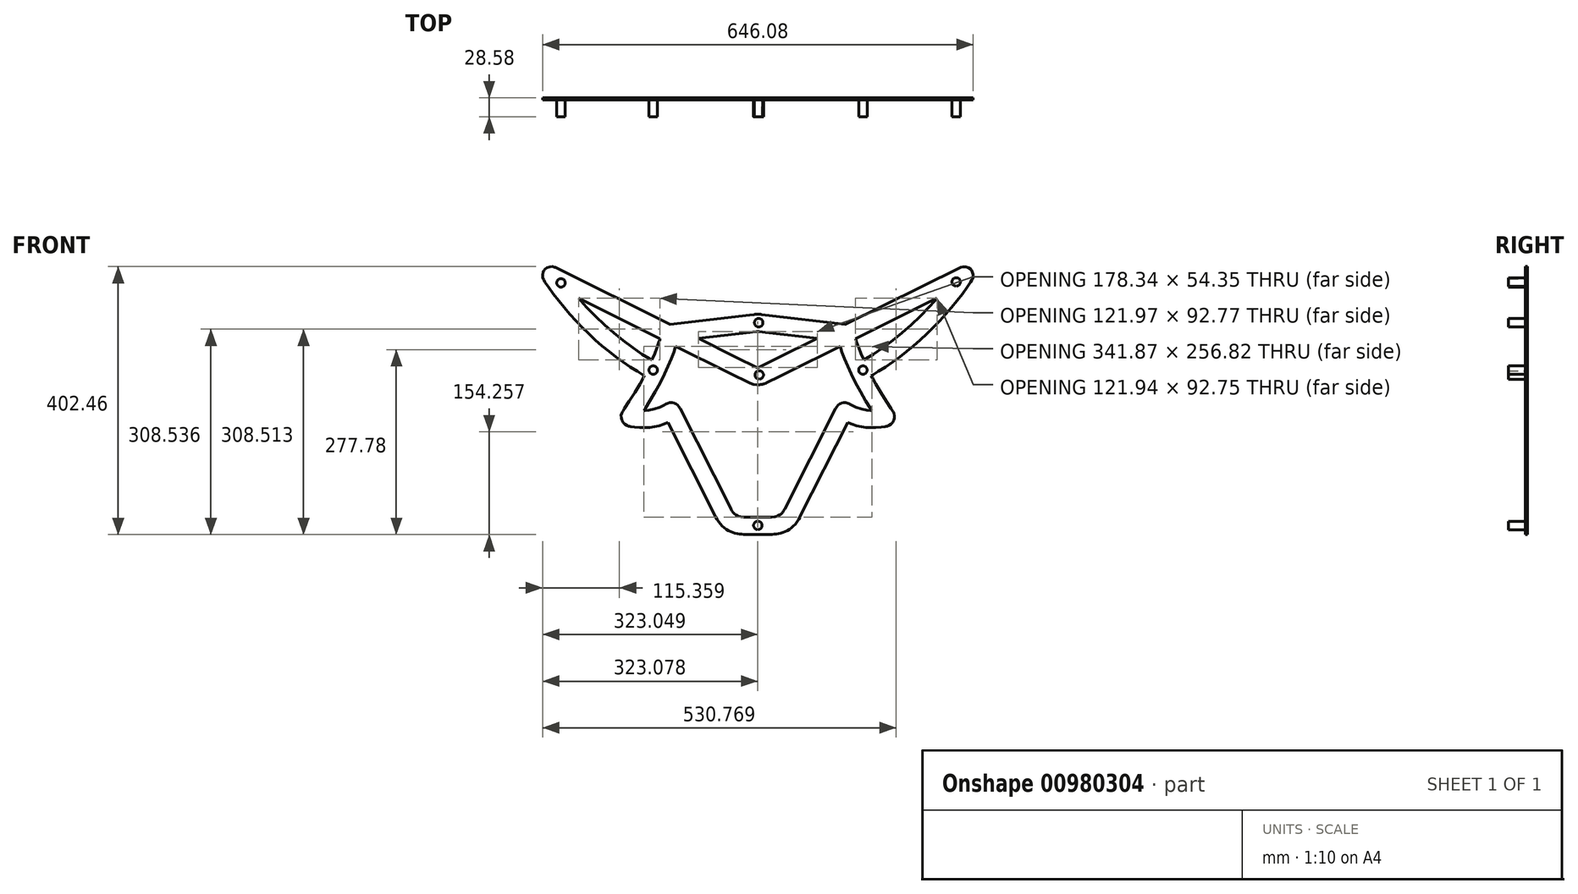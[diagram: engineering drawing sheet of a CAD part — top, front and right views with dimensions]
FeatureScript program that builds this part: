
annotation { "Feature Type Name" : "Feature", "Feature Type Description" : "" }
export const myFeature = defineFeature(function(context is Context, id is Id, definition is map)
    precondition{}
    {
        {
            var Q0;
            Q0=qCreatedBy(makeId("Front.planeOp"),FACE);
            var sketch = newSketch(context, id + "F0", { "sketchPlane" : qUnion([Q0])});
            skLineSegment(sketch, "E0", {"start": v(158.95, 60.93) * mm, "end": v(157.84, 63.41) * mm});
            skLineSegment(sketch, "E1", {"start": v(157.84, 63.41) * mm, "end": v(154.67, 70.92) * mm});
            skLineSegment(sketch, "E2", {"start": v(154.67, 70.92) * mm, "end": v(151.24, 79.68) * mm});
            skLineSegment(sketch, "E3", {"start": v(151.24, 79.68) * mm, "end": v(148.62, 87.1) * mm});
            skLineSegment(sketch, "E4", {"start": v(148.62, 87.1) * mm, "end": v(147.19, 91.58) * mm});
            skLineSegment(sketch, "E5", {"start": v(147.19, 91.58) * mm, "end": v(146.76, 93.08) * mm});
            skLineSegment(sketch, "E6", {"start": v(146.76, 93.08) * mm, "end": v(268.7, 153.68) * mm});
            skLineSegment(sketch, "E7", {"start": v(268.7, 153.68) * mm, "end": v(265.73, 150.2) * mm});
            skLineSegment(sketch, "E8", {"start": v(265.73, 150.2) * mm, "end": v(256.53, 140.02) * mm});
            skLineSegment(sketch, "E9", {"start": v(256.53, 140.02) * mm, "end": v(243.66, 126.71) * mm});
            skLineSegment(sketch, "E10", {"start": v(243.66, 126.71) * mm, "end": v(230.23, 113.88) * mm});
            skLineSegment(sketch, "E11", {"start": v(230.23, 113.88) * mm, "end": v(216.35, 101.64) * mm});
            skLineSegment(sketch, "E12", {"start": v(216.35, 101.64) * mm, "end": v(202.16, 90.1) * mm});
            skLineSegment(sketch, "E13", {"start": v(202.16, 90.1) * mm, "end": v(187.77, 79.4) * mm});
            skLineSegment(sketch, "E14", {"start": v(187.77, 79.4) * mm, "end": v(173.33, 69.63) * mm});
            skLineSegment(sketch, "E15", {"start": v(173.33, 69.63) * mm, "end": v(162.6, 63) * mm});
            skLineSegment(sketch, "E16", {"start": v(162.6, 63) * mm, "end": v(158.95, 60.93) * mm});
            skLineSegment(sketch, "E17", {"start": v(138.45, -5.62) * mm, "end": v(137.73, -5.16) * mm});
            skLineSegment(sketch, "E18", {"start": v(137.73, -5.16) * mm, "end": v(135.36, -4.11) * mm});
            skLineSegment(sketch, "E19", {"start": v(135.36, -4.11) * mm, "end": v(132.1, -3.33) * mm});
            skLineSegment(sketch, "E20", {"start": v(132.1, -3.33) * mm, "end": v(128.75, -3.29) * mm});
            skLineSegment(sketch, "E21", {"start": v(128.75, -3.29) * mm, "end": v(126.25, -3.73) * mm});
            skLineSegment(sketch, "E22", {"start": v(126.25, -3.73) * mm, "end": v(125.46, -4) * mm});
            skLineSegment(sketch, "E23", {"start": v(125.46, -4) * mm, "end": v(124.74, -4.23) * mm});
            skLineSegment(sketch, "E24", {"start": v(124.74, -4.23) * mm, "end": v(122.7, -5.25) * mm});
            skLineSegment(sketch, "E25", {"start": v(122.7, -5.25) * mm, "end": v(120.27, -7.02) * mm});
            skLineSegment(sketch, "E26", {"start": v(120.27, -7.02) * mm, "end": v(118.26, -9.24) * mm});
            skLineSegment(sketch, "E27", {"start": v(118.26, -9.24) * mm, "end": v(117.04, -11.17) * mm});
            skLineSegment(sketch, "E28", {"start": v(117.04, -11.17) * mm, "end": v(116.73, -11.86) * mm});
            skLineSegment(sketch, "E29", {"start": v(116.73, -11.86) * mm, "end": v(40.26, -162.76) * mm});
            skLineSegment(sketch, "E30", {"start": v(40.26, -162.76) * mm, "end": v(39.9, -163.51) * mm});
            skLineSegment(sketch, "E31", {"start": v(39.9, -163.51) * mm, "end": v(38.73, -165.7) * mm});
            skLineSegment(sketch, "E32", {"start": v(38.73, -165.7) * mm, "end": v(36.98, -168.27) * mm});
            skLineSegment(sketch, "E33", {"start": v(36.98, -168.27) * mm, "end": v(34.91, -170.44) * mm});
            skLineSegment(sketch, "E34", {"start": v(34.91, -170.44) * mm, "end": v(32.4, -172.21) * mm});
            skLineSegment(sketch, "E35", {"start": v(32.4, -172.21) * mm, "end": v(29.3, -173.6) * mm});
            skLineSegment(sketch, "E36", {"start": v(29.3, -173.6) * mm, "end": v(25.54, -174.59) * mm});
            skLineSegment(sketch, "E37", {"start": v(25.54, -174.59) * mm, "end": v(20.97, -175.19) * mm});
            skLineSegment(sketch, "E38", {"start": v(20.97, -175.19) * mm, "end": v(16.85, -175.38) * mm});
            skLineSegment(sketch, "E39", {"start": v(16.85, -175.38) * mm, "end": v(15.48, -175.38) * mm});
            skLineSegment(sketch, "E40", {"start": v(15.48, -175.38) * mm, "end": v(-15.4, -175.38) * mm});
            skLineSegment(sketch, "E41", {"start": v(-15.4, -175.38) * mm, "end": v(-16.77, -175.38) * mm});
            skLineSegment(sketch, "E42", {"start": v(-16.77, -175.38) * mm, "end": v(-20.88, -175.19) * mm});
            skLineSegment(sketch, "E43", {"start": v(-20.88, -175.19) * mm, "end": v(-25.46, -174.58) * mm});
            skLineSegment(sketch, "E44", {"start": v(-25.46, -174.58) * mm, "end": v(-29.24, -173.58) * mm});
            skLineSegment(sketch, "E45", {"start": v(-29.24, -173.58) * mm, "end": v(-32.34, -172.17) * mm});
            skLineSegment(sketch, "E46", {"start": v(-32.34, -172.17) * mm, "end": v(-34.88, -170.34) * mm});
            skLineSegment(sketch, "E47", {"start": v(-34.88, -170.34) * mm, "end": v(-36.99, -168.1) * mm});
            skLineSegment(sketch, "E48", {"start": v(-36.99, -168.1) * mm, "end": v(-38.78, -165.45) * mm});
            skLineSegment(sketch, "E49", {"start": v(-38.78, -165.45) * mm, "end": v(-40, -163.16) * mm});
            skLineSegment(sketch, "E50", {"start": v(-40, -163.16) * mm, "end": v(-40.37, -162.38) * mm});
            skLineSegment(sketch, "E51", {"start": v(-40.37, -162.38) * mm, "end": v(-116.64, -11.86) * mm});
            skLineSegment(sketch, "E52", {"start": v(-116.64, -11.86) * mm, "end": v(-116.96, -11.17) * mm});
            skLineSegment(sketch, "E53", {"start": v(-116.96, -11.17) * mm, "end": v(-118.19, -9.23) * mm});
            skLineSegment(sketch, "E54", {"start": v(-118.19, -9.23) * mm, "end": v(-120.2, -7) * mm});
            skLineSegment(sketch, "E55", {"start": v(-120.2, -7) * mm, "end": v(-122.63, -5.24) * mm});
            skLineSegment(sketch, "E56", {"start": v(-122.63, -5.24) * mm, "end": v(-124.68, -4.23) * mm});
            skLineSegment(sketch, "E57", {"start": v(-124.68, -4.23) * mm, "end": v(-125.4, -3.99) * mm});
            skLineSegment(sketch, "E58", {"start": v(-125.4, -3.99) * mm, "end": v(-126.2, -3.72) * mm});
            skLineSegment(sketch, "E59", {"start": v(-126.2, -3.72) * mm, "end": v(-128.7, -3.29) * mm});
            skLineSegment(sketch, "E60", {"start": v(-128.7, -3.29) * mm, "end": v(-132.04, -3.34) * mm});
            skLineSegment(sketch, "E61", {"start": v(-132.04, -3.34) * mm, "end": v(-135.3, -4.12) * mm});
            skLineSegment(sketch, "E62", {"start": v(-135.3, -4.12) * mm, "end": v(-137.66, -5.17) * mm});
            skLineSegment(sketch, "E63", {"start": v(-137.66, -5.17) * mm, "end": v(-138.37, -5.62) * mm});
            skLineSegment(sketch, "E64", {"start": v(-138.37, -5.62) * mm, "end": v(-140.4, -6.9) * mm});
            skLineSegment(sketch, "E65", {"start": v(-140.4, -6.9) * mm, "end": v(-146.9, -10.04) * mm});
            skLineSegment(sketch, "E66", {"start": v(-146.9, -10.04) * mm, "end": v(-155.32, -12.85) * mm});
            skLineSegment(sketch, "E67", {"start": v(-155.32, -12.85) * mm, "end": v(-163.4, -14.36) * mm});
            skLineSegment(sketch, "E68", {"start": v(-163.4, -14.36) * mm, "end": v(-169.02, -14.84) * mm});
            skLineSegment(sketch, "E69", {"start": v(-169.02, -14.84) * mm, "end": v(-170.9, -14.87) * mm});
            skLineSegment(sketch, "E70", {"start": v(-170.9, -14.87) * mm, "end": v(-168.58, -11.29) * mm});
            skLineSegment(sketch, "E71", {"start": v(-168.58, -11.29) * mm, "end": v(-161.87, -0.4) * mm});
            skLineSegment(sketch, "E72", {"start": v(-161.87, -0.4) * mm, "end": v(-153.74, 13.64) * mm});
            skLineSegment(sketch, "E73", {"start": v(-153.74, 13.64) * mm, "end": v(-146.5, 27.1) * mm});
            skLineSegment(sketch, "E74", {"start": v(-146.5, 27.1) * mm, "end": v(-140.15, 39.86) * mm});
            skLineSegment(sketch, "E75", {"start": v(-140.15, 39.86) * mm, "end": v(-134.66, 51.8) * mm});
            skLineSegment(sketch, "E76", {"start": v(-134.66, 51.8) * mm, "end": v(-130.02, 62.78) * mm});
            skLineSegment(sketch, "E77", {"start": v(-130.02, 62.78) * mm, "end": v(-126.23, 72.7) * mm});
            skLineSegment(sketch, "E78", {"start": v(-126.23, 72.7) * mm, "end": v(-123.96, 79.22) * mm});
            skLineSegment(sketch, "E79", {"start": v(-123.96, 79.22) * mm, "end": v(-123.27, 81.4) * mm});
            skLineSegment(sketch, "E80", {"start": v(-123.27, 81.4) * mm, "end": v(-44.12, 42.07) * mm});
            skLineSegment(sketch, "E81", {"start": v(-44.12, 42.07) * mm, "end": v(-44.12, 42.07) * mm});
            skLineSegment(sketch, "E82", {"start": v(-44.12, 42.07) * mm, "end": v(-41.36, 40.7) * mm});
            skLineSegment(sketch, "E83", {"start": v(-41.36, 40.7) * mm, "end": v(-12.8, 26.5) * mm});
            skLineSegment(sketch, "E84", {"start": v(-12.8, 26.5) * mm, "end": v(-11.81, 26.02) * mm});
            skLineSegment(sketch, "E85", {"start": v(-11.81, 26.02) * mm, "end": v(-6.56, 24.28) * mm});
            skLineSegment(sketch, "E86", {"start": v(-6.56, 24.28) * mm, "end": v(-1.6, 23.52) * mm});
            skLineSegment(sketch, "E87", {"start": v(-1.6, 23.52) * mm, "end": v(0.05, 23.52) * mm});
            skLineSegment(sketch, "E88", {"start": v(0.05, 23.52) * mm, "end": v(0.42, 23.52) * mm});
            skLineSegment(sketch, "E89", {"start": v(0.42, 23.52) * mm, "end": v(2.26, 23.7) * mm});
            skLineSegment(sketch, "E90", {"start": v(2.26, 23.7) * mm, "end": v(4.09, 23.99) * mm});
            skLineSegment(sketch, "E91", {"start": v(4.09, 23.99) * mm, "end": v(4.46, 24.05) * mm});
            skLineSegment(sketch, "E92", {"start": v(4.46, 24.05) * mm, "end": v(4.63, 24.08) * mm});
            skLineSegment(sketch, "E93", {"start": v(4.63, 24.08) * mm, "end": v(6.44, 24.26) * mm});
            skLineSegment(sketch, "E94", {"start": v(6.44, 24.26) * mm, "end": v(6.62, 24.3) * mm});
            skLineSegment(sketch, "E95", {"start": v(6.62, 24.3) * mm, "end": v(6.78, 24.34) * mm});
            skLineSegment(sketch, "E96", {"start": v(6.78, 24.34) * mm, "end": v(8.34, 24.93) * mm});
            skLineSegment(sketch, "E97", {"start": v(8.34, 24.93) * mm, "end": v(8.5, 24.98) * mm});
            skLineSegment(sketch, "E98", {"start": v(8.5, 24.98) * mm, "end": v(8.87, 25.09) * mm});
            skLineSegment(sketch, "E99", {"start": v(8.87, 25.09) * mm, "end": v(10.72, 25.67) * mm});
            skLineSegment(sketch, "E100", {"start": v(10.72, 25.67) * mm, "end": v(12.53, 26.37) * mm});
            skLineSegment(sketch, "E101", {"start": v(12.53, 26.37) * mm, "end": v(12.88, 26.54) * mm});
            skLineSegment(sketch, "E102", {"start": v(12.88, 26.54) * mm, "end": v(32.7, 36.4) * mm});
            skLineSegment(sketch, "E103", {"start": v(32.7, 36.4) * mm, "end": v(44.15, 42.08) * mm});
            skLineSegment(sketch, "E104", {"start": v(44.15, 42.08) * mm, "end": v(44.14, 42.08) * mm});
            skLineSegment(sketch, "E105", {"start": v(44.14, 42.08) * mm, "end": v(123.34, 81.44) * mm});
            skLineSegment(sketch, "E106", {"start": v(123.34, 81.44) * mm, "end": v(124.03, 79.25) * mm});
            skLineSegment(sketch, "E107", {"start": v(124.03, 79.25) * mm, "end": v(126.3, 72.72) * mm});
            skLineSegment(sketch, "E108", {"start": v(126.3, 72.72) * mm, "end": v(130.09, 62.8) * mm});
            skLineSegment(sketch, "E109", {"start": v(130.09, 62.8) * mm, "end": v(134.72, 51.81) * mm});
            skLineSegment(sketch, "E110", {"start": v(134.72, 51.81) * mm, "end": v(140.21, 39.87) * mm});
            skLineSegment(sketch, "E111", {"start": v(140.21, 39.87) * mm, "end": v(146.57, 27.1) * mm});
            skLineSegment(sketch, "E112", {"start": v(146.57, 27.1) * mm, "end": v(153.81, 13.65) * mm});
            skLineSegment(sketch, "E113", {"start": v(153.81, 13.65) * mm, "end": v(161.94, -0.39) * mm});
            skLineSegment(sketch, "E114", {"start": v(161.94, -0.39) * mm, "end": v(168.65, -11.29) * mm});
            skLineSegment(sketch, "E115", {"start": v(168.65, -11.29) * mm, "end": v(170.97, -14.87) * mm});
            skLineSegment(sketch, "E116", {"start": v(170.97, -14.87) * mm, "end": v(169.1, -14.84) * mm});
            skLineSegment(sketch, "E117", {"start": v(169.1, -14.84) * mm, "end": v(163.48, -14.36) * mm});
            skLineSegment(sketch, "E118", {"start": v(163.48, -14.36) * mm, "end": v(155.4, -12.85) * mm});
            skLineSegment(sketch, "E119", {"start": v(155.4, -12.85) * mm, "end": v(146.97, -10.04) * mm});
            skLineSegment(sketch, "E120", {"start": v(146.97, -10.04) * mm, "end": v(140.48, -6.89) * mm});
            skLineSegment(sketch, "E121", {"start": v(140.48, -6.89) * mm, "end": v(138.45, -5.62) * mm});
            skLineSegment(sketch, "E122", {"start": v(-268.67, 153.67) * mm, "end": v(-146.7, 93.05) * mm});
            skLineSegment(sketch, "E123", {"start": v(-146.7, 93.05) * mm, "end": v(-147.13, 91.55) * mm});
            skLineSegment(sketch, "E124", {"start": v(-147.13, 91.55) * mm, "end": v(-148.56, 87.07) * mm});
            skLineSegment(sketch, "E125", {"start": v(-148.56, 87.07) * mm, "end": v(-151.18, 79.64) * mm});
            skLineSegment(sketch, "E126", {"start": v(-151.18, 79.64) * mm, "end": v(-154.61, 70.88) * mm});
            skLineSegment(sketch, "E127", {"start": v(-154.61, 70.88) * mm, "end": v(-157.78, 63.38) * mm});
            skLineSegment(sketch, "E128", {"start": v(-157.78, 63.38) * mm, "end": v(-158.89, 60.9) * mm});
            skLineSegment(sketch, "E129", {"start": v(-158.89, 60.9) * mm, "end": v(-162.54, 62.97) * mm});
            skLineSegment(sketch, "E130", {"start": v(-162.54, 62.97) * mm, "end": v(-173.27, 69.6) * mm});
            skLineSegment(sketch, "E131", {"start": v(-173.27, 69.6) * mm, "end": v(-187.71, 79.36) * mm});
            skLineSegment(sketch, "E132", {"start": v(-187.71, 79.36) * mm, "end": v(-202.1, 90.07) * mm});
            skLineSegment(sketch, "E133", {"start": v(-202.1, 90.07) * mm, "end": v(-216.3, 101.6) * mm});
            skLineSegment(sketch, "E134", {"start": v(-216.3, 101.6) * mm, "end": v(-230.18, 113.85) * mm});
            skLineSegment(sketch, "E135", {"start": v(-230.18, 113.85) * mm, "end": v(-243.62, 126.69) * mm});
            skLineSegment(sketch, "E136", {"start": v(-243.62, 126.69) * mm, "end": v(-256.49, 140) * mm});
            skLineSegment(sketch, "E137", {"start": v(-256.49, 140) * mm, "end": v(-265.7, 150.19) * mm});
            skLineSegment(sketch, "E138", {"start": v(-265.7, 150.19) * mm, "end": v(-268.67, 153.67) * mm});
            skLineSegment(sketch, "E139", {"start": v(-11.4, 102.56) * mm, "end": v(-11.4, 102.56) * mm});
            skLineSegment(sketch, "E140", {"start": v(-11.4, 102.56) * mm, "end": v(-7.8, 103) * mm});
            skLineSegment(sketch, "E141", {"start": v(-7.8, 103) * mm, "end": v(-2.03, 103.68) * mm});
            skLineSegment(sketch, "E142", {"start": v(-2.03, 103.68) * mm, "end": v(-1.68, 103.72) * mm});
            skLineSegment(sketch, "E143", {"start": v(-1.68, 103.72) * mm, "end": v(1.76, 103.73) * mm});
            skLineSegment(sketch, "E144", {"start": v(1.76, 103.73) * mm, "end": v(2.1, 103.68) * mm});
            skLineSegment(sketch, "E145", {"start": v(2.1, 103.68) * mm, "end": v(6.66, 103.14) * mm});
            skLineSegment(sketch, "E146", {"start": v(6.66, 103.14) * mm, "end": v(11.48, 102.56) * mm});
            skLineSegment(sketch, "E147", {"start": v(11.48, 102.56) * mm, "end": v(11.48, 102.56) * mm});
            skLineSegment(sketch, "E148", {"start": v(11.48, 102.56) * mm, "end": v(89.18, 93.31) * mm});
            skLineSegment(sketch, "E149", {"start": v(89.18, 93.31) * mm, "end": v(27.84, 62.83) * mm});
            skLineSegment(sketch, "E150", {"start": v(27.84, 62.83) * mm, "end": v(1.36, 49.69) * mm});
            skLineSegment(sketch, "E151", {"start": v(1.36, 49.69) * mm, "end": v(1.25, 49.63) * mm});
            skLineSegment(sketch, "E152", {"start": v(1.25, 49.63) * mm, "end": v(0.3, 49.37) * mm});
            skLineSegment(sketch, "E153", {"start": v(0.3, 49.37) * mm, "end": v(-0.02, 49.37) * mm});
            skLineSegment(sketch, "E154", {"start": v(-0.02, 49.37) * mm, "end": v(-0.13, 49.38) * mm});
            skLineSegment(sketch, "E155", {"start": v(-0.13, 49.38) * mm, "end": v(-1.24, 49.64) * mm});
            skLineSegment(sketch, "E156", {"start": v(-1.24, 49.64) * mm, "end": v(-1.34, 49.7) * mm});
            skLineSegment(sketch, "E157", {"start": v(-1.34, 49.7) * mm, "end": v(-32.64, 65.22) * mm});
            skLineSegment(sketch, "E158", {"start": v(-32.64, 65.22) * mm, "end": v(-89.16, 93.3) * mm});
            skLineSegment(sketch, "E159", {"start": v(-89.16, 93.3) * mm, "end": v(-11.4, 102.56) * mm});
            skLineSegment(sketch, "E160", {"start": v(319.65, 196.96) * mm, "end": v(318.9, 197.75) * mm});
            skLineSegment(sketch, "E161", {"start": v(318.9, 197.75) * mm, "end": v(316.1, 199.63) * mm});
            skLineSegment(sketch, "E162", {"start": v(316.1, 199.63) * mm, "end": v(311.99, 201.03) * mm});
            skLineSegment(sketch, "E163", {"start": v(311.99, 201.03) * mm, "end": v(307.64, 201.1) * mm});
            skLineSegment(sketch, "E164", {"start": v(307.64, 201.1) * mm, "end": v(304.38, 200.27) * mm});
            skLineSegment(sketch, "E165", {"start": v(304.38, 200.27) * mm, "end": v(303.4, 199.78) * mm});
            skLineSegment(sketch, "E166", {"start": v(303.4, 199.78) * mm, "end": v(131.42, 114.3) * mm});
            skLineSegment(sketch, "E167", {"start": v(131.42, 114.3) * mm, "end": v(11.14, 128.63) * mm});
            skLineSegment(sketch, "E168", {"start": v(11.14, 128.63) * mm, "end": v(5.2, 129.34) * mm});
            skLineSegment(sketch, "E169", {"start": v(5.2, 129.34) * mm, "end": v(4.78, 129.39) * mm});
            skLineSegment(sketch, "E170", {"start": v(4.78, 129.39) * mm, "end": v(0.47, 129.64) * mm});
            skLineSegment(sketch, "E171", {"start": v(0.47, 129.64) * mm, "end": v(0.04, 129.64) * mm});
            skLineSegment(sketch, "E172", {"start": v(0.04, 129.64) * mm, "end": v(-0.4, 129.64) * mm});
            skLineSegment(sketch, "E173", {"start": v(-0.4, 129.64) * mm, "end": v(-4.71, 129.39) * mm});
            skLineSegment(sketch, "E174", {"start": v(-4.71, 129.39) * mm, "end": v(-5.14, 129.34) * mm});
            skLineSegment(sketch, "E175", {"start": v(-5.14, 129.34) * mm, "end": v(-12.44, 128.46) * mm});
            skLineSegment(sketch, "E176", {"start": v(-12.44, 128.46) * mm, "end": v(-131.4, 114.3) * mm});
            skLineSegment(sketch, "E177", {"start": v(-131.4, 114.3) * mm, "end": v(-303.73, 199.95) * mm});
            skLineSegment(sketch, "E178", {"start": v(-303.73, 199.95) * mm, "end": v(-304.7, 200.43) * mm});
            skLineSegment(sketch, "E179", {"start": v(-304.7, 200.43) * mm, "end": v(-307.9, 201.23) * mm});
            skLineSegment(sketch, "E180", {"start": v(-307.9, 201.23) * mm, "end": v(-312.18, 201.11) * mm});
            skLineSegment(sketch, "E181", {"start": v(-312.18, 201.11) * mm, "end": v(-316.2, 199.66) * mm});
            skLineSegment(sketch, "E182", {"start": v(-316.2, 199.66) * mm, "end": v(-318.9, 197.74) * mm});
            skLineSegment(sketch, "E183", {"start": v(-318.9, 197.74) * mm, "end": v(-319.63, 196.94) * mm});
            skLineSegment(sketch, "E184", {"start": v(-319.63, 196.94) * mm, "end": v(-319.9, 196.62) * mm});
            skLineSegment(sketch, "E185", {"start": v(-319.9, 196.62) * mm, "end": v(-320.58, 195.82) * mm});
            skLineSegment(sketch, "E186", {"start": v(-320.58, 195.82) * mm, "end": v(-322.1, 192.98) * mm});
            skLineSegment(sketch, "E187", {"start": v(-322.1, 192.98) * mm, "end": v(-323.04, 188.93) * mm});
            skLineSegment(sketch, "E188", {"start": v(-323.04, 188.93) * mm, "end": v(-322.68, 184.79) * mm});
            skLineSegment(sketch, "E189", {"start": v(-322.68, 184.79) * mm, "end": v(-321.58, 181.76) * mm});
            skLineSegment(sketch, "E190", {"start": v(-321.58, 181.76) * mm, "end": v(-321.01, 180.87) * mm});
            skLineSegment(sketch, "E191", {"start": v(-321.01, 180.87) * mm, "end": v(-319.35, 178.24) * mm});
            skLineSegment(sketch, "E192", {"start": v(-319.35, 178.24) * mm, "end": v(-314.17, 170.47) * mm});
            skLineSegment(sketch, "E193", {"start": v(-314.17, 170.47) * mm, "end": v(-306.8, 160.1) * mm});
            skLineSegment(sketch, "E194", {"start": v(-306.8, 160.1) * mm, "end": v(-298.95, 149.78) * mm});
            skLineSegment(sketch, "E195", {"start": v(-298.95, 149.78) * mm, "end": v(-290.66, 139.55) * mm});
            skLineSegment(sketch, "E196", {"start": v(-290.66, 139.55) * mm, "end": v(-281.95, 129.47) * mm});
            skLineSegment(sketch, "E197", {"start": v(-281.95, 129.47) * mm, "end": v(-272.87, 119.55) * mm});
            skLineSegment(sketch, "E198", {"start": v(-272.87, 119.55) * mm, "end": v(-263.46, 109.83) * mm});
            skLineSegment(sketch, "E199", {"start": v(-263.46, 109.83) * mm, "end": v(-253.76, 100.36) * mm});
            skLineSegment(sketch, "E200", {"start": v(-253.76, 100.36) * mm, "end": v(-243.8, 91.16) * mm});
            skLineSegment(sketch, "E201", {"start": v(-243.8, 91.16) * mm, "end": v(-233.64, 82.28) * mm});
            skLineSegment(sketch, "E202", {"start": v(-233.64, 82.28) * mm, "end": v(-223.29, 73.74) * mm});
            skLineSegment(sketch, "E203", {"start": v(-223.29, 73.74) * mm, "end": v(-212.8, 65.6) * mm});
            skLineSegment(sketch, "E204", {"start": v(-212.8, 65.6) * mm, "end": v(-202.2, 57.86) * mm});
            skLineSegment(sketch, "E205", {"start": v(-202.2, 57.86) * mm, "end": v(-191.55, 50.59) * mm});
            skLineSegment(sketch, "E206", {"start": v(-191.55, 50.59) * mm, "end": v(-180.87, 43.8) * mm});
            skLineSegment(sketch, "E207", {"start": v(-180.87, 43.8) * mm, "end": v(-172.9, 39.07) * mm});
            skLineSegment(sketch, "E208", {"start": v(-172.9, 39.07) * mm, "end": v(-170.2, 37.56) * mm});
            skLineSegment(sketch, "E209", {"start": v(-170.2, 37.56) * mm, "end": v(-171.83, 34.44) * mm});
            skLineSegment(sketch, "E210", {"start": v(-171.83, 34.44) * mm, "end": v(-176.9, 25.2) * mm});
            skLineSegment(sketch, "E211", {"start": v(-176.9, 25.2) * mm, "end": v(-184.47, 12.17) * mm});
            skLineSegment(sketch, "E212", {"start": v(-184.47, 12.17) * mm, "end": v(-192.96, -1.42) * mm});
            skLineSegment(sketch, "E213", {"start": v(-192.96, -1.42) * mm, "end": v(-200, -12) * mm});
            skLineSegment(sketch, "E214", {"start": v(-200, -12) * mm, "end": v(-202.42, -15.46) * mm});
            skLineSegment(sketch, "E215", {"start": v(-202.42, -15.46) * mm, "end": v(-202.95, -16.22) * mm});
            skLineSegment(sketch, "E216", {"start": v(-202.95, -16.22) * mm, "end": v(-204.17, -18.79) * mm});
            skLineSegment(sketch, "E217", {"start": v(-204.17, -18.79) * mm, "end": v(-205.02, -22.37) * mm});
            skLineSegment(sketch, "E218", {"start": v(-205.02, -22.37) * mm, "end": v(-204.96, -26.06) * mm});
            skLineSegment(sketch, "E219", {"start": v(-204.96, -26.06) * mm, "end": v(-204.33, -28.83) * mm});
            skLineSegment(sketch, "E220", {"start": v(-204.33, -28.83) * mm, "end": v(-203.98, -29.69) * mm});
            skLineSegment(sketch, "E221", {"start": v(-203.98, -29.69) * mm, "end": v(-203.62, -30.55) * mm});
            skLineSegment(sketch, "E222", {"start": v(-203.62, -30.55) * mm, "end": v(-202.13, -32.95) * mm});
            skLineSegment(sketch, "E223", {"start": v(-202.13, -32.95) * mm, "end": v(-199.58, -35.6) * mm});
            skLineSegment(sketch, "E224", {"start": v(-199.58, -35.6) * mm, "end": v(-196.44, -37.55) * mm});
            skLineSegment(sketch, "E225", {"start": v(-196.44, -37.55) * mm, "end": v(-193.76, -38.52) * mm});
            skLineSegment(sketch, "E226", {"start": v(-193.76, -38.52) * mm, "end": v(-192.84, -38.7) * mm});
            skLineSegment(sketch, "E227", {"start": v(-192.84, -38.7) * mm, "end": v(-190.87, -39.05) * mm});
            skLineSegment(sketch, "E228", {"start": v(-190.87, -39.05) * mm, "end": v(-184.9, -39.87) * mm});
            skLineSegment(sketch, "E229", {"start": v(-184.9, -39.87) * mm, "end": v(-177.13, -40.52) * mm});
            skLineSegment(sketch, "E230", {"start": v(-177.13, -40.52) * mm, "end": v(-169.57, -40.62) * mm});
            skLineSegment(sketch, "E231", {"start": v(-169.57, -40.62) * mm, "end": v(-162.21, -40.17) * mm});
            skLineSegment(sketch, "E232", {"start": v(-162.21, -40.17) * mm, "end": v(-155.06, -39.19) * mm});
            skLineSegment(sketch, "E233", {"start": v(-155.06, -39.19) * mm, "end": v(-148.12, -37.66) * mm});
            skLineSegment(sketch, "E234", {"start": v(-148.12, -37.66) * mm, "end": v(-141.4, -35.6) * mm});
            skLineSegment(sketch, "E235", {"start": v(-141.4, -35.6) * mm, "end": v(-136.49, -33.71) * mm});
            skLineSegment(sketch, "E236", {"start": v(-136.49, -33.71) * mm, "end": v(-134.9, -33) * mm});
            skLineSegment(sketch, "E237", {"start": v(-134.9, -33) * mm, "end": v(-63.6, -173.68) * mm});
            skLineSegment(sketch, "E238", {"start": v(-63.6, -173.68) * mm, "end": v(-63.08, -174.8) * mm});
            skLineSegment(sketch, "E239", {"start": v(-63.08, -174.8) * mm, "end": v(-61.33, -178.06) * mm});
            skLineSegment(sketch, "E240", {"start": v(-61.33, -178.06) * mm, "end": v(-58.85, -181.95) * mm});
            skLineSegment(sketch, "E241", {"start": v(-58.85, -181.95) * mm, "end": v(-56.18, -185.4) * mm});
            skLineSegment(sketch, "E242", {"start": v(-56.18, -185.4) * mm, "end": v(-53.34, -188.4) * mm});
            skLineSegment(sketch, "E243", {"start": v(-53.34, -188.4) * mm, "end": v(-50.37, -191.01) * mm});
            skLineSegment(sketch, "E244", {"start": v(-50.37, -191.01) * mm, "end": v(-47.29, -193.25) * mm});
            skLineSegment(sketch, "E245", {"start": v(-47.29, -193.25) * mm, "end": v(-44.11, -195.14) * mm});
            skLineSegment(sketch, "E246", {"start": v(-44.11, -195.14) * mm, "end": v(-40.87, -196.71) * mm});
            skLineSegment(sketch, "E247", {"start": v(-40.87, -196.71) * mm, "end": v(-37.59, -198) * mm});
            skLineSegment(sketch, "E248", {"start": v(-37.59, -198) * mm, "end": v(-34.28, -199.02) * mm});
            skLineSegment(sketch, "E249", {"start": v(-34.28, -199.02) * mm, "end": v(-30.98, -199.81) * mm});
            skLineSegment(sketch, "E250", {"start": v(-30.98, -199.81) * mm, "end": v(-27.7, -200.4) * mm});
            skLineSegment(sketch, "E251", {"start": v(-27.7, -200.4) * mm, "end": v(-24.5, -200.8) * mm});
            skLineSegment(sketch, "E252", {"start": v(-24.5, -200.8) * mm, "end": v(-21.35, -201.06) * mm});
            skLineSegment(sketch, "E253", {"start": v(-21.35, -201.06) * mm, "end": v(-18.3, -201.2) * mm});
            skLineSegment(sketch, "E254", {"start": v(-18.3, -201.2) * mm, "end": v(-16.12, -201.23) * mm});
            skLineSegment(sketch, "E255", {"start": v(-16.12, -201.23) * mm, "end": v(-15.4, -201.23) * mm});
            skLineSegment(sketch, "E256", {"start": v(-15.4, -201.23) * mm, "end": v(15.48, -201.23) * mm});
            skLineSegment(sketch, "E257", {"start": v(15.48, -201.23) * mm, "end": v(16.2, -201.23) * mm});
            skLineSegment(sketch, "E258", {"start": v(16.2, -201.23) * mm, "end": v(18.4, -201.2) * mm});
            skLineSegment(sketch, "E259", {"start": v(18.4, -201.2) * mm, "end": v(21.43, -201.06) * mm});
            skLineSegment(sketch, "E260", {"start": v(21.43, -201.06) * mm, "end": v(24.58, -200.8) * mm});
            skLineSegment(sketch, "E261", {"start": v(24.58, -200.8) * mm, "end": v(27.79, -200.4) * mm});
            skLineSegment(sketch, "E262", {"start": v(27.79, -200.4) * mm, "end": v(31.06, -199.82) * mm});
            skLineSegment(sketch, "E263", {"start": v(31.06, -199.82) * mm, "end": v(34.36, -199.04) * mm});
            skLineSegment(sketch, "E264", {"start": v(34.36, -199.04) * mm, "end": v(37.65, -198.03) * mm});
            skLineSegment(sketch, "E265", {"start": v(37.65, -198.03) * mm, "end": v(40.93, -196.76) * mm});
            skLineSegment(sketch, "E266", {"start": v(40.93, -196.76) * mm, "end": v(44.16, -195.2) * mm});
            skLineSegment(sketch, "E267", {"start": v(44.16, -195.2) * mm, "end": v(47.33, -193.34) * mm});
            skLineSegment(sketch, "E268", {"start": v(47.33, -193.34) * mm, "end": v(50.4, -191.13) * mm});
            skLineSegment(sketch, "E269", {"start": v(50.4, -191.13) * mm, "end": v(53.34, -188.56) * mm});
            skLineSegment(sketch, "E270", {"start": v(53.34, -188.56) * mm, "end": v(56.16, -185.6) * mm});
            skLineSegment(sketch, "E271", {"start": v(56.16, -185.6) * mm, "end": v(58.8, -182.2) * mm});
            skLineSegment(sketch, "E272", {"start": v(58.8, -182.2) * mm, "end": v(61.25, -178.37) * mm});
            skLineSegment(sketch, "E273", {"start": v(61.25, -178.37) * mm, "end": v(62.98, -175.16) * mm});
            skLineSegment(sketch, "E274", {"start": v(62.98, -175.16) * mm, "end": v(63.49, -174.06) * mm});
            skLineSegment(sketch, "E275", {"start": v(63.49, -174.06) * mm, "end": v(134.98, -33) * mm});
            skLineSegment(sketch, "E276", {"start": v(134.98, -33) * mm, "end": v(136.57, -33.72) * mm});
            skLineSegment(sketch, "E277", {"start": v(136.57, -33.72) * mm, "end": v(141.47, -35.6) * mm});
            skLineSegment(sketch, "E278", {"start": v(141.47, -35.6) * mm, "end": v(148.18, -37.67) * mm});
            skLineSegment(sketch, "E279", {"start": v(148.18, -37.67) * mm, "end": v(155.12, -39.2) * mm});
            skLineSegment(sketch, "E280", {"start": v(155.12, -39.2) * mm, "end": v(162.27, -40.18) * mm});
            skLineSegment(sketch, "E281", {"start": v(162.27, -40.18) * mm, "end": v(169.63, -40.62) * mm});
            skLineSegment(sketch, "E282", {"start": v(169.63, -40.62) * mm, "end": v(177.2, -40.52) * mm});
            skLineSegment(sketch, "E283", {"start": v(177.2, -40.52) * mm, "end": v(184.98, -39.87) * mm});
            skLineSegment(sketch, "E284", {"start": v(184.98, -39.87) * mm, "end": v(190.98, -39.04) * mm});
            skLineSegment(sketch, "E285", {"start": v(190.98, -39.04) * mm, "end": v(192.96, -38.68) * mm});
            skLineSegment(sketch, "E286", {"start": v(192.96, -38.68) * mm, "end": v(193.87, -38.52) * mm});
            skLineSegment(sketch, "E287", {"start": v(193.87, -38.52) * mm, "end": v(196.53, -37.55) * mm});
            skLineSegment(sketch, "E288", {"start": v(196.53, -37.55) * mm, "end": v(199.65, -35.61) * mm});
            skLineSegment(sketch, "E289", {"start": v(199.65, -35.61) * mm, "end": v(202.2, -32.97) * mm});
            skLineSegment(sketch, "E290", {"start": v(202.2, -32.97) * mm, "end": v(203.69, -30.57) * mm});
            skLineSegment(sketch, "E291", {"start": v(203.69, -30.57) * mm, "end": v(204.04, -29.7) * mm});
            skLineSegment(sketch, "E292", {"start": v(204.04, -29.7) * mm, "end": v(204.4, -28.85) * mm});
            skLineSegment(sketch, "E293", {"start": v(204.4, -28.85) * mm, "end": v(205.04, -26.1) * mm});
            skLineSegment(sketch, "E294", {"start": v(205.04, -26.1) * mm, "end": v(205.1, -22.4) * mm});
            skLineSegment(sketch, "E295", {"start": v(205.1, -22.4) * mm, "end": v(204.24, -18.8) * mm});
            skLineSegment(sketch, "E296", {"start": v(204.24, -18.8) * mm, "end": v(203.02, -16.21) * mm});
            skLineSegment(sketch, "E297", {"start": v(203.02, -16.21) * mm, "end": v(202.49, -15.44) * mm});
            skLineSegment(sketch, "E298", {"start": v(202.49, -15.44) * mm, "end": v(200.06, -11.97) * mm});
            skLineSegment(sketch, "E299", {"start": v(200.06, -11.97) * mm, "end": v(193.03, -1.4) * mm});
            skLineSegment(sketch, "E300", {"start": v(193.03, -1.4) * mm, "end": v(184.53, 12.2) * mm});
            skLineSegment(sketch, "E301", {"start": v(184.53, 12.2) * mm, "end": v(176.95, 25.22) * mm});
            skLineSegment(sketch, "E302", {"start": v(176.95, 25.22) * mm, "end": v(171.88, 34.48) * mm});
            skLineSegment(sketch, "E303", {"start": v(171.88, 34.48) * mm, "end": v(170.26, 37.6) * mm});
            skLineSegment(sketch, "E304", {"start": v(170.26, 37.6) * mm, "end": v(172.95, 39.1) * mm});
            skLineSegment(sketch, "E305", {"start": v(172.95, 39.1) * mm, "end": v(180.93, 43.84) * mm});
            skLineSegment(sketch, "E306", {"start": v(180.93, 43.84) * mm, "end": v(191.6, 50.62) * mm});
            skLineSegment(sketch, "E307", {"start": v(191.6, 50.62) * mm, "end": v(202.25, 57.9) * mm});
            skLineSegment(sketch, "E308", {"start": v(202.25, 57.9) * mm, "end": v(212.85, 65.62) * mm});
            skLineSegment(sketch, "E309", {"start": v(212.85, 65.62) * mm, "end": v(223.33, 73.77) * mm});
            skLineSegment(sketch, "E310", {"start": v(223.33, 73.77) * mm, "end": v(233.68, 82.3) * mm});
            skLineSegment(sketch, "E311", {"start": v(233.68, 82.3) * mm, "end": v(243.85, 91.19) * mm});
            skLineSegment(sketch, "E312", {"start": v(243.85, 91.19) * mm, "end": v(253.8, 100.38) * mm});
            skLineSegment(sketch, "E313", {"start": v(253.8, 100.38) * mm, "end": v(263.5, 109.85) * mm});
            skLineSegment(sketch, "E314", {"start": v(263.5, 109.85) * mm, "end": v(272.9, 119.57) * mm});
            skLineSegment(sketch, "E315", {"start": v(272.9, 119.57) * mm, "end": v(281.98, 129.48) * mm});
            skLineSegment(sketch, "E316", {"start": v(281.98, 129.48) * mm, "end": v(290.68, 139.57) * mm});
            skLineSegment(sketch, "E317", {"start": v(290.68, 139.57) * mm, "end": v(298.97, 149.78) * mm});
            skLineSegment(sketch, "E318", {"start": v(298.97, 149.78) * mm, "end": v(306.82, 160.1) * mm});
            skLineSegment(sketch, "E319", {"start": v(306.82, 160.1) * mm, "end": v(314.18, 170.46) * mm});
            skLineSegment(sketch, "E320", {"start": v(314.18, 170.46) * mm, "end": v(319.36, 178.22) * mm});
            skLineSegment(sketch, "E321", {"start": v(319.36, 178.22) * mm, "end": v(321.02, 180.86) * mm});
            skLineSegment(sketch, "E322", {"start": v(321.02, 180.86) * mm, "end": v(321.6, 181.76) * mm});
            skLineSegment(sketch, "E323", {"start": v(321.6, 181.76) * mm, "end": v(322.72, 184.87) * mm});
            skLineSegment(sketch, "E324", {"start": v(322.72, 184.87) * mm, "end": v(323.04, 189.13) * mm});
            skLineSegment(sketch, "E325", {"start": v(323.04, 189.13) * mm, "end": v(322, 193.28) * mm});
            skLineSegment(sketch, "E326", {"start": v(322, 193.28) * mm, "end": v(320.38, 196.16) * mm});
            skLineSegment(sketch, "E327", {"start": v(320.38, 196.16) * mm, "end": v(319.65, 196.96) * mm});
            skSolve(sketch);
        }
        {
            var Q0;
            Q0=makeQuery(id+"F0.imprint","IMPRINT",FACE,{"disambiguationData":[TD([[makeQuery(id+"F0.imprint","IMPRINT",EDGE,{"derivedFrom":sQuery(id+"F0.wireOp",EDGE,"E0")}),1.0]])]});
            extrude(context, id + "F1", {"entities" : qUnion([Q0]), "depth" : 3.17 * mm, "offsetDistance" : 25.4 * mm});
        }
        {
            var Q0;
            Q0=makeQuery(id+"F1.opExtrude","CAP_FACE",FACE,{"disambiguationData":[OSD([sQuery(id+"F0.wireOp",EDGE,"E0"),sQuery(id+"F0.wireOp",EDGE,"E1"),sQuery(id+"F0.wireOp",EDGE,"E2"),sQuery(id+"F0.wireOp",EDGE,"E3"),sQuery(id+"F0.wireOp",EDGE,"E4"),sQuery(id+"F0.wireOp",EDGE,"E5"),sQuery(id+"F0.wireOp",EDGE,"E6"),sQuery(id+"F0.wireOp",EDGE,"E7"),sQuery(id+"F0.wireOp",EDGE,"E8"),sQuery(id+"F0.wireOp",EDGE,"E9"),sQuery(id+"F0.wireOp",EDGE,"E10"),sQuery(id+"F0.wireOp",EDGE,"E11"),sQuery(id+"F0.wireOp",EDGE,"E12"),sQuery(id+"F0.wireOp",EDGE,"E13"),sQuery(id+"F0.wireOp",EDGE,"E14"),sQuery(id+"F0.wireOp",EDGE,"E15"),sQuery(id+"F0.wireOp",EDGE,"E16"),sQuery(id+"F0.wireOp",EDGE,"E17"),sQuery(id+"F0.wireOp",EDGE,"E18"),sQuery(id+"F0.wireOp",EDGE,"E19"),sQuery(id+"F0.wireOp",EDGE,"E20"),sQuery(id+"F0.wireOp",EDGE,"E21"),sQuery(id+"F0.wireOp",EDGE,"E22"),sQuery(id+"F0.wireOp",EDGE,"E23"),sQuery(id+"F0.wireOp",EDGE,"E24"),sQuery(id+"F0.wireOp",EDGE,"E25"),sQuery(id+"F0.wireOp",EDGE,"E26"),sQuery(id+"F0.wireOp",EDGE,"E27"),sQuery(id+"F0.wireOp",EDGE,"E28"),sQuery(id+"F0.wireOp",EDGE,"E29"),sQuery(id+"F0.wireOp",EDGE,"E30"),sQuery(id+"F0.wireOp",EDGE,"E31"),sQuery(id+"F0.wireOp",EDGE,"E32"),sQuery(id+"F0.wireOp",EDGE,"E33"),sQuery(id+"F0.wireOp",EDGE,"E34"),sQuery(id+"F0.wireOp",EDGE,"E35"),sQuery(id+"F0.wireOp",EDGE,"E36"),sQuery(id+"F0.wireOp",EDGE,"E37"),sQuery(id+"F0.wireOp",EDGE,"E38"),sQuery(id+"F0.wireOp",EDGE,"E39"),sQuery(id+"F0.wireOp",EDGE,"E40"),sQuery(id+"F0.wireOp",EDGE,"E41"),sQuery(id+"F0.wireOp",EDGE,"E42"),sQuery(id+"F0.wireOp",EDGE,"E43"),sQuery(id+"F0.wireOp",EDGE,"E44"),sQuery(id+"F0.wireOp",EDGE,"E45"),sQuery(id+"F0.wireOp",EDGE,"E46"),sQuery(id+"F0.wireOp",EDGE,"E47"),sQuery(id+"F0.wireOp",EDGE,"E48"),sQuery(id+"F0.wireOp",EDGE,"E49"),sQuery(id+"F0.wireOp",EDGE,"E50"),sQuery(id+"F0.wireOp",EDGE,"E51"),sQuery(id+"F0.wireOp",EDGE,"E52"),sQuery(id+"F0.wireOp",EDGE,"E53"),sQuery(id+"F0.wireOp",EDGE,"E54"),sQuery(id+"F0.wireOp",EDGE,"E55"),sQuery(id+"F0.wireOp",EDGE,"E56"),sQuery(id+"F0.wireOp",EDGE,"E57"),sQuery(id+"F0.wireOp",EDGE,"E58"),sQuery(id+"F0.wireOp",EDGE,"E59"),sQuery(id+"F0.wireOp",EDGE,"E60"),sQuery(id+"F0.wireOp",EDGE,"E61"),sQuery(id+"F0.wireOp",EDGE,"E62"),sQuery(id+"F0.wireOp",EDGE,"E63"),sQuery(id+"F0.wireOp",EDGE,"E64"),sQuery(id+"F0.wireOp",EDGE,"E65"),sQuery(id+"F0.wireOp",EDGE,"E66"),sQuery(id+"F0.wireOp",EDGE,"E67"),sQuery(id+"F0.wireOp",EDGE,"E68"),sQuery(id+"F0.wireOp",EDGE,"E69"),sQuery(id+"F0.wireOp",EDGE,"E70"),sQuery(id+"F0.wireOp",EDGE,"E71"),sQuery(id+"F0.wireOp",EDGE,"E72"),sQuery(id+"F0.wireOp",EDGE,"E73"),sQuery(id+"F0.wireOp",EDGE,"E74"),sQuery(id+"F0.wireOp",EDGE,"E75"),sQuery(id+"F0.wireOp",EDGE,"E76"),sQuery(id+"F0.wireOp",EDGE,"E77"),sQuery(id+"F0.wireOp",EDGE,"E78"),sQuery(id+"F0.wireOp",EDGE,"E79"),sQuery(id+"F0.wireOp",EDGE,"E80"),sQuery(id+"F0.wireOp",EDGE,"E81"),sQuery(id+"F0.wireOp",EDGE,"E82"),sQuery(id+"F0.wireOp",EDGE,"E83"),sQuery(id+"F0.wireOp",EDGE,"E84"),sQuery(id+"F0.wireOp",EDGE,"E85"),sQuery(id+"F0.wireOp",EDGE,"E86"),sQuery(id+"F0.wireOp",EDGE,"E87"),sQuery(id+"F0.wireOp",EDGE,"E88"),sQuery(id+"F0.wireOp",EDGE,"E89"),sQuery(id+"F0.wireOp",EDGE,"E90"),sQuery(id+"F0.wireOp",EDGE,"E91"),sQuery(id+"F0.wireOp",EDGE,"E92"),sQuery(id+"F0.wireOp",EDGE,"E93"),sQuery(id+"F0.wireOp",EDGE,"E94"),sQuery(id+"F0.wireOp",EDGE,"E95"),sQuery(id+"F0.wireOp",EDGE,"E96"),sQuery(id+"F0.wireOp",EDGE,"E97"),sQuery(id+"F0.wireOp",EDGE,"E98"),sQuery(id+"F0.wireOp",EDGE,"E99"),sQuery(id+"F0.wireOp",EDGE,"E100"),sQuery(id+"F0.wireOp",EDGE,"E101"),sQuery(id+"F0.wireOp",EDGE,"E102"),sQuery(id+"F0.wireOp",EDGE,"E103"),sQuery(id+"F0.wireOp",EDGE,"E104"),sQuery(id+"F0.wireOp",EDGE,"E105"),sQuery(id+"F0.wireOp",EDGE,"E106"),sQuery(id+"F0.wireOp",EDGE,"E107"),sQuery(id+"F0.wireOp",EDGE,"E108"),sQuery(id+"F0.wireOp",EDGE,"E109"),sQuery(id+"F0.wireOp",EDGE,"E110"),sQuery(id+"F0.wireOp",EDGE,"E111"),sQuery(id+"F0.wireOp",EDGE,"E112"),sQuery(id+"F0.wireOp",EDGE,"E113"),sQuery(id+"F0.wireOp",EDGE,"E114"),sQuery(id+"F0.wireOp",EDGE,"E115"),sQuery(id+"F0.wireOp",EDGE,"E116"),sQuery(id+"F0.wireOp",EDGE,"E117"),sQuery(id+"F0.wireOp",EDGE,"E118"),sQuery(id+"F0.wireOp",EDGE,"E119"),sQuery(id+"F0.wireOp",EDGE,"E120"),sQuery(id+"F0.wireOp",EDGE,"E121"),sQuery(id+"F0.wireOp",EDGE,"E122"),sQuery(id+"F0.wireOp",EDGE,"E123"),sQuery(id+"F0.wireOp",EDGE,"E124"),sQuery(id+"F0.wireOp",EDGE,"E125"),sQuery(id+"F0.wireOp",EDGE,"E126"),sQuery(id+"F0.wireOp",EDGE,"E127"),sQuery(id+"F0.wireOp",EDGE,"E128"),sQuery(id+"F0.wireOp",EDGE,"E129"),sQuery(id+"F0.wireOp",EDGE,"E130"),sQuery(id+"F0.wireOp",EDGE,"E131"),sQuery(id+"F0.wireOp",EDGE,"E132"),sQuery(id+"F0.wireOp",EDGE,"E133"),sQuery(id+"F0.wireOp",EDGE,"E134"),sQuery(id+"F0.wireOp",EDGE,"E135"),sQuery(id+"F0.wireOp",EDGE,"E136"),sQuery(id+"F0.wireOp",EDGE,"E137"),sQuery(id+"F0.wireOp",EDGE,"E138"),sQuery(id+"F0.wireOp",EDGE,"E139"),sQuery(id+"F0.wireOp",EDGE,"E140"),sQuery(id+"F0.wireOp",EDGE,"E141"),sQuery(id+"F0.wireOp",EDGE,"E142"),sQuery(id+"F0.wireOp",EDGE,"E143"),sQuery(id+"F0.wireOp",EDGE,"E144"),sQuery(id+"F0.wireOp",EDGE,"E145"),sQuery(id+"F0.wireOp",EDGE,"E146"),sQuery(id+"F0.wireOp",EDGE,"E147"),sQuery(id+"F0.wireOp",EDGE,"E148"),sQuery(id+"F0.wireOp",EDGE,"E149"),sQuery(id+"F0.wireOp",EDGE,"E150"),sQuery(id+"F0.wireOp",EDGE,"E151"),sQuery(id+"F0.wireOp",EDGE,"E152"),sQuery(id+"F0.wireOp",EDGE,"E153"),sQuery(id+"F0.wireOp",EDGE,"E154"),sQuery(id+"F0.wireOp",EDGE,"E155"),sQuery(id+"F0.wireOp",EDGE,"E156"),sQuery(id+"F0.wireOp",EDGE,"E157"),sQuery(id+"F0.wireOp",EDGE,"E158"),sQuery(id+"F0.wireOp",EDGE,"E159"),sQuery(id+"F0.wireOp",EDGE,"E160"),sQuery(id+"F0.wireOp",EDGE,"E161"),sQuery(id+"F0.wireOp",EDGE,"E162"),sQuery(id+"F0.wireOp",EDGE,"E163"),sQuery(id+"F0.wireOp",EDGE,"E164"),sQuery(id+"F0.wireOp",EDGE,"E165"),sQuery(id+"F0.wireOp",EDGE,"E166"),sQuery(id+"F0.wireOp",EDGE,"E167"),sQuery(id+"F0.wireOp",EDGE,"E168"),sQuery(id+"F0.wireOp",EDGE,"E169"),sQuery(id+"F0.wireOp",EDGE,"E170"),sQuery(id+"F0.wireOp",EDGE,"E171"),sQuery(id+"F0.wireOp",EDGE,"E172"),sQuery(id+"F0.wireOp",EDGE,"E173"),sQuery(id+"F0.wireOp",EDGE,"E174"),sQuery(id+"F0.wireOp",EDGE,"E175"),sQuery(id+"F0.wireOp",EDGE,"E176"),sQuery(id+"F0.wireOp",EDGE,"E177"),sQuery(id+"F0.wireOp",EDGE,"E178"),sQuery(id+"F0.wireOp",EDGE,"E179"),sQuery(id+"F0.wireOp",EDGE,"E180"),sQuery(id+"F0.wireOp",EDGE,"E181"),sQuery(id+"F0.wireOp",EDGE,"E182"),sQuery(id+"F0.wireOp",EDGE,"E183"),sQuery(id+"F0.wireOp",EDGE,"E184"),sQuery(id+"F0.wireOp",EDGE,"E185"),sQuery(id+"F0.wireOp",EDGE,"E186"),sQuery(id+"F0.wireOp",EDGE,"E187"),sQuery(id+"F0.wireOp",EDGE,"E188"),sQuery(id+"F0.wireOp",EDGE,"E189"),sQuery(id+"F0.wireOp",EDGE,"E190"),sQuery(id+"F0.wireOp",EDGE,"E191"),sQuery(id+"F0.wireOp",EDGE,"E192"),sQuery(id+"F0.wireOp",EDGE,"E193"),sQuery(id+"F0.wireOp",EDGE,"E194"),sQuery(id+"F0.wireOp",EDGE,"E195"),sQuery(id+"F0.wireOp",EDGE,"E196"),sQuery(id+"F0.wireOp",EDGE,"E197"),sQuery(id+"F0.wireOp",EDGE,"E198"),sQuery(id+"F0.wireOp",EDGE,"E199"),sQuery(id+"F0.wireOp",EDGE,"E200"),sQuery(id+"F0.wireOp",EDGE,"E201"),sQuery(id+"F0.wireOp",EDGE,"E202"),sQuery(id+"F0.wireOp",EDGE,"E203"),sQuery(id+"F0.wireOp",EDGE,"E204"),sQuery(id+"F0.wireOp",EDGE,"E205"),sQuery(id+"F0.wireOp",EDGE,"E206"),sQuery(id+"F0.wireOp",EDGE,"E207"),sQuery(id+"F0.wireOp",EDGE,"E208"),sQuery(id+"F0.wireOp",EDGE,"E209"),sQuery(id+"F0.wireOp",EDGE,"E210"),sQuery(id+"F0.wireOp",EDGE,"E211"),sQuery(id+"F0.wireOp",EDGE,"E212"),sQuery(id+"F0.wireOp",EDGE,"E213"),sQuery(id+"F0.wireOp",EDGE,"E214"),sQuery(id+"F0.wireOp",EDGE,"E215"),sQuery(id+"F0.wireOp",EDGE,"E216"),sQuery(id+"F0.wireOp",EDGE,"E217"),sQuery(id+"F0.wireOp",EDGE,"E218"),sQuery(id+"F0.wireOp",EDGE,"E219"),sQuery(id+"F0.wireOp",EDGE,"E220"),sQuery(id+"F0.wireOp",EDGE,"E221"),sQuery(id+"F0.wireOp",EDGE,"E222"),sQuery(id+"F0.wireOp",EDGE,"E223"),sQuery(id+"F0.wireOp",EDGE,"E224"),sQuery(id+"F0.wireOp",EDGE,"E225"),sQuery(id+"F0.wireOp",EDGE,"E226"),sQuery(id+"F0.wireOp",EDGE,"E227"),sQuery(id+"F0.wireOp",EDGE,"E228"),sQuery(id+"F0.wireOp",EDGE,"E229"),sQuery(id+"F0.wireOp",EDGE,"E230"),sQuery(id+"F0.wireOp",EDGE,"E231"),sQuery(id+"F0.wireOp",EDGE,"E232"),sQuery(id+"F0.wireOp",EDGE,"E233"),sQuery(id+"F0.wireOp",EDGE,"E234"),sQuery(id+"F0.wireOp",EDGE,"E235"),sQuery(id+"F0.wireOp",EDGE,"E236"),sQuery(id+"F0.wireOp",EDGE,"E237"),sQuery(id+"F0.wireOp",EDGE,"E238"),sQuery(id+"F0.wireOp",EDGE,"E239"),sQuery(id+"F0.wireOp",EDGE,"E240"),sQuery(id+"F0.wireOp",EDGE,"E241"),sQuery(id+"F0.wireOp",EDGE,"E242"),sQuery(id+"F0.wireOp",EDGE,"E243"),sQuery(id+"F0.wireOp",EDGE,"E244"),sQuery(id+"F0.wireOp",EDGE,"E245"),sQuery(id+"F0.wireOp",EDGE,"E246"),sQuery(id+"F0.wireOp",EDGE,"E247"),sQuery(id+"F0.wireOp",EDGE,"E248"),sQuery(id+"F0.wireOp",EDGE,"E249"),sQuery(id+"F0.wireOp",EDGE,"E250"),sQuery(id+"F0.wireOp",EDGE,"E251"),sQuery(id+"F0.wireOp",EDGE,"E252"),sQuery(id+"F0.wireOp",EDGE,"E253"),sQuery(id+"F0.wireOp",EDGE,"E254"),sQuery(id+"F0.wireOp",EDGE,"E255"),sQuery(id+"F0.wireOp",EDGE,"E256"),sQuery(id+"F0.wireOp",EDGE,"E257"),sQuery(id+"F0.wireOp",EDGE,"E258"),sQuery(id+"F0.wireOp",EDGE,"E259"),sQuery(id+"F0.wireOp",EDGE,"E260"),sQuery(id+"F0.wireOp",EDGE,"E261"),sQuery(id+"F0.wireOp",EDGE,"E262"),sQuery(id+"F0.wireOp",EDGE,"E263"),sQuery(id+"F0.wireOp",EDGE,"E264"),sQuery(id+"F0.wireOp",EDGE,"E265"),sQuery(id+"F0.wireOp",EDGE,"E266"),sQuery(id+"F0.wireOp",EDGE,"E267"),sQuery(id+"F0.wireOp",EDGE,"E268"),sQuery(id+"F0.wireOp",EDGE,"E269"),sQuery(id+"F0.wireOp",EDGE,"E270"),sQuery(id+"F0.wireOp",EDGE,"E271"),sQuery(id+"F0.wireOp",EDGE,"E272"),sQuery(id+"F0.wireOp",EDGE,"E273"),sQuery(id+"F0.wireOp",EDGE,"E274"),sQuery(id+"F0.wireOp",EDGE,"E275"),sQuery(id+"F0.wireOp",EDGE,"E276"),sQuery(id+"F0.wireOp",EDGE,"E277"),sQuery(id+"F0.wireOp",EDGE,"E278"),sQuery(id+"F0.wireOp",EDGE,"E279"),sQuery(id+"F0.wireOp",EDGE,"E280"),sQuery(id+"F0.wireOp",EDGE,"E281"),sQuery(id+"F0.wireOp",EDGE,"E282"),sQuery(id+"F0.wireOp",EDGE,"E283"),sQuery(id+"F0.wireOp",EDGE,"E284"),sQuery(id+"F0.wireOp",EDGE,"E285"),sQuery(id+"F0.wireOp",EDGE,"E286"),sQuery(id+"F0.wireOp",EDGE,"E287"),sQuery(id+"F0.wireOp",EDGE,"E288"),sQuery(id+"F0.wireOp",EDGE,"E289"),sQuery(id+"F0.wireOp",EDGE,"E290"),sQuery(id+"F0.wireOp",EDGE,"E291"),sQuery(id+"F0.wireOp",EDGE,"E292"),sQuery(id+"F0.wireOp",EDGE,"E293"),sQuery(id+"F0.wireOp",EDGE,"E294"),sQuery(id+"F0.wireOp",EDGE,"E295"),sQuery(id+"F0.wireOp",EDGE,"E296"),sQuery(id+"F0.wireOp",EDGE,"E297"),sQuery(id+"F0.wireOp",EDGE,"E298"),sQuery(id+"F0.wireOp",EDGE,"E299"),sQuery(id+"F0.wireOp",EDGE,"E300"),sQuery(id+"F0.wireOp",EDGE,"E301"),sQuery(id+"F0.wireOp",EDGE,"E302"),sQuery(id+"F0.wireOp",EDGE,"E303"),sQuery(id+"F0.wireOp",EDGE,"E304"),sQuery(id+"F0.wireOp",EDGE,"E305"),sQuery(id+"F0.wireOp",EDGE,"E306"),sQuery(id+"F0.wireOp",EDGE,"E307"),sQuery(id+"F0.wireOp",EDGE,"E308"),sQuery(id+"F0.wireOp",EDGE,"E309"),sQuery(id+"F0.wireOp",EDGE,"E310"),sQuery(id+"F0.wireOp",EDGE,"E311"),sQuery(id+"F0.wireOp",EDGE,"E312"),sQuery(id+"F0.wireOp",EDGE,"E313"),sQuery(id+"F0.wireOp",EDGE,"E314"),sQuery(id+"F0.wireOp",EDGE,"E315"),sQuery(id+"F0.wireOp",EDGE,"E316"),sQuery(id+"F0.wireOp",EDGE,"E317"),sQuery(id+"F0.wireOp",EDGE,"E318"),sQuery(id+"F0.wireOp",EDGE,"E319"),sQuery(id+"F0.wireOp",EDGE,"E320"),sQuery(id+"F0.wireOp",EDGE,"E321"),sQuery(id+"F0.wireOp",EDGE,"E322"),sQuery(id+"F0.wireOp",EDGE,"E323"),sQuery(id+"F0.wireOp",EDGE,"E324"),sQuery(id+"F0.wireOp",EDGE,"E325"),sQuery(id+"F0.wireOp",EDGE,"E326"),sQuery(id+"F0.wireOp",EDGE,"E327")])],"isStart":false});
            var sketch = newSketch(context, id + "F2", { "sketchPlane" : qUnion([Q0])});
            skCircle(sketch, "E328", {"center": v(-295.33, 176.85) * mm, "radius": 6.35 * mm});
            skCircle(sketch, "E329", {"center": v(297.69, 178.24) * mm, "radius": 6.35 * mm});
            skCircle(sketch, "E330", {"center": v(-156.88, 45.83) * mm, "radius": 6.35 * mm});
            skPoint(sketch, "E330.centerSnap0", {"position": v(-137.4, 45.83) * mm});
            skCircle(sketch, "E331", {"center": v(157.66, 45.83) * mm, "radius": 6.35 * mm});
            skCircle(sketch, "E332", {"center": v(0.04, -187.5) * mm, "radius": 6.35 * mm});
            skPoint(sketch, "E332.centerSnap0", {"position": v(0.04, -201.23) * mm});
            skCircle(sketch, "E333", {"center": v(1.36, 116.96) * mm, "radius": 6.35 * mm});
            skCircle(sketch, "E334", {"center": v(2.1, 38.54) * mm, "radius": 6.35 * mm});
            skSolve(sketch);
        }
        {
            var Q0;
            Q0=makeQuery(id+"F2.imprint","IMPRINT",FACE,{"disambiguationData":[TD([[makeQuery(id+"F2.imprint","IMPRINT",EDGE,{"derivedFrom":sQuery(id+"F2.wireOp",EDGE,"E328")}),1.0]])]});
            var Q1;
            Q1=makeQuery(id+"F2.imprint","IMPRINT",FACE,{"disambiguationData":[TD([[makeQuery(id+"F2.imprint","IMPRINT",EDGE,{"derivedFrom":sQuery(id+"F2.wireOp",EDGE,"E333")}),1.0]])]});
            var Q2;
            Q2=makeQuery(id+"F2.imprint","IMPRINT",FACE,{"disambiguationData":[TD([[makeQuery(id+"F2.imprint","IMPRINT",EDGE,{"derivedFrom":sQuery(id+"F2.wireOp",EDGE,"E330")}),1.0]])]});
            var Q3;
            Q3=makeQuery(id+"F2.imprint","IMPRINT",FACE,{"disambiguationData":[TD([[makeQuery(id+"F2.imprint","IMPRINT",EDGE,{"derivedFrom":sQuery(id+"F2.wireOp",EDGE,"E334")}),1.0]])]});
            var Q4;
            Q4=makeQuery(id+"F2.imprint","IMPRINT",FACE,{"disambiguationData":[TD([[makeQuery(id+"F2.imprint","IMPRINT",EDGE,{"derivedFrom":sQuery(id+"F2.wireOp",EDGE,"E332")}),1.0]])]});
            var Q5;
            Q5=makeQuery(id+"F2.imprint","IMPRINT",FACE,{"disambiguationData":[TD([[makeQuery(id+"F2.imprint","IMPRINT",EDGE,{"derivedFrom":sQuery(id+"F2.wireOp",EDGE,"E331")}),1.0]])]});
            var Q6;
            Q6=makeQuery(id+"F2.imprint","IMPRINT",FACE,{"disambiguationData":[TD([[makeQuery(id+"F2.imprint","IMPRINT",EDGE,{"derivedFrom":sQuery(id+"F2.wireOp",EDGE,"E329")}),1.0]])]});
            extrude(context, id + "F3", {"entities" : qUnion([Q0, Q1, Q2, Q3, Q4, Q5, Q6]), "depth" : 25.4 * mm, "offsetDistance" : 25.4 * mm});
        }
    });
